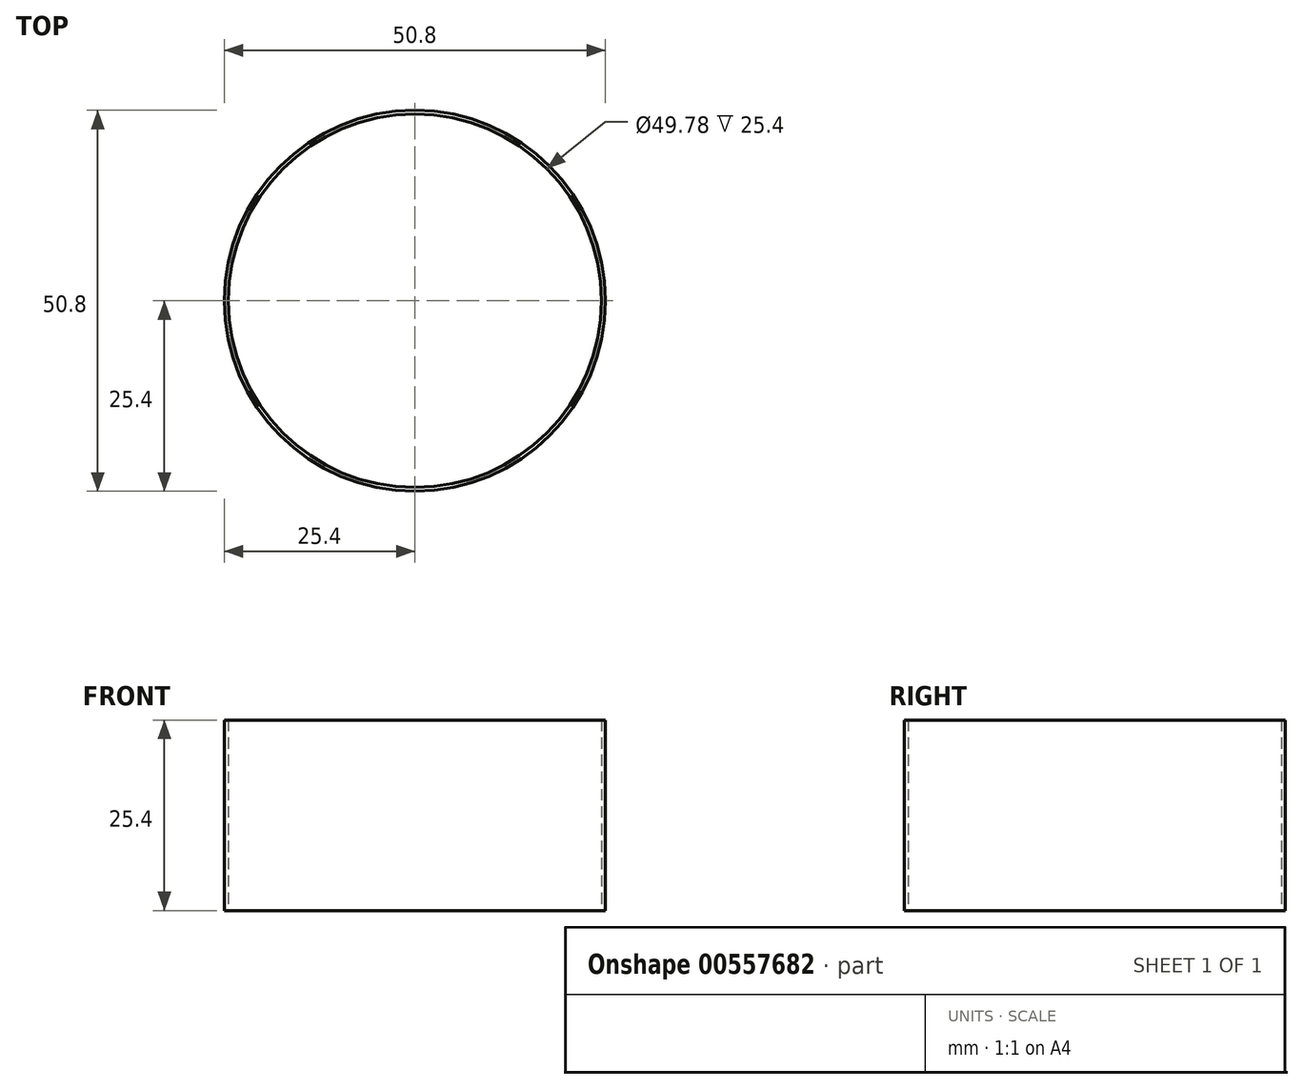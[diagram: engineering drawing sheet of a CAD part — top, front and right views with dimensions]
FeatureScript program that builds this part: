
annotation { "Feature Type Name" : "Feature", "Feature Type Description" : "" }
export const myFeature = defineFeature(function(context is Context, id is Id, definition is map)
    precondition{}
    {
        {
            var Q0;
            Q0=qCreatedBy(makeId("Top.planeOp"),FACE);
            var sketch = newSketch(context, id + "F0", { "sketchPlane" : qUnion([Q0])});
            skCircle(sketch, "E0", {"center": v(0, 0) * mm, "radius": 25.4 * mm});
            skCircle(sketch, "E1", {"center": v(0, 0) * mm, "radius": 24.9 * mm});
            skSolve(sketch);
        }
        {
            var Q0;
            Q0 = qSketchRegion(id + "F0", true);
            extrude(context, id + "F1", {"entities" : qUnion([Q0]), "depth" : 25.4 * mm, "offsetDistance" : 25.4 * mm});
        }
    });
